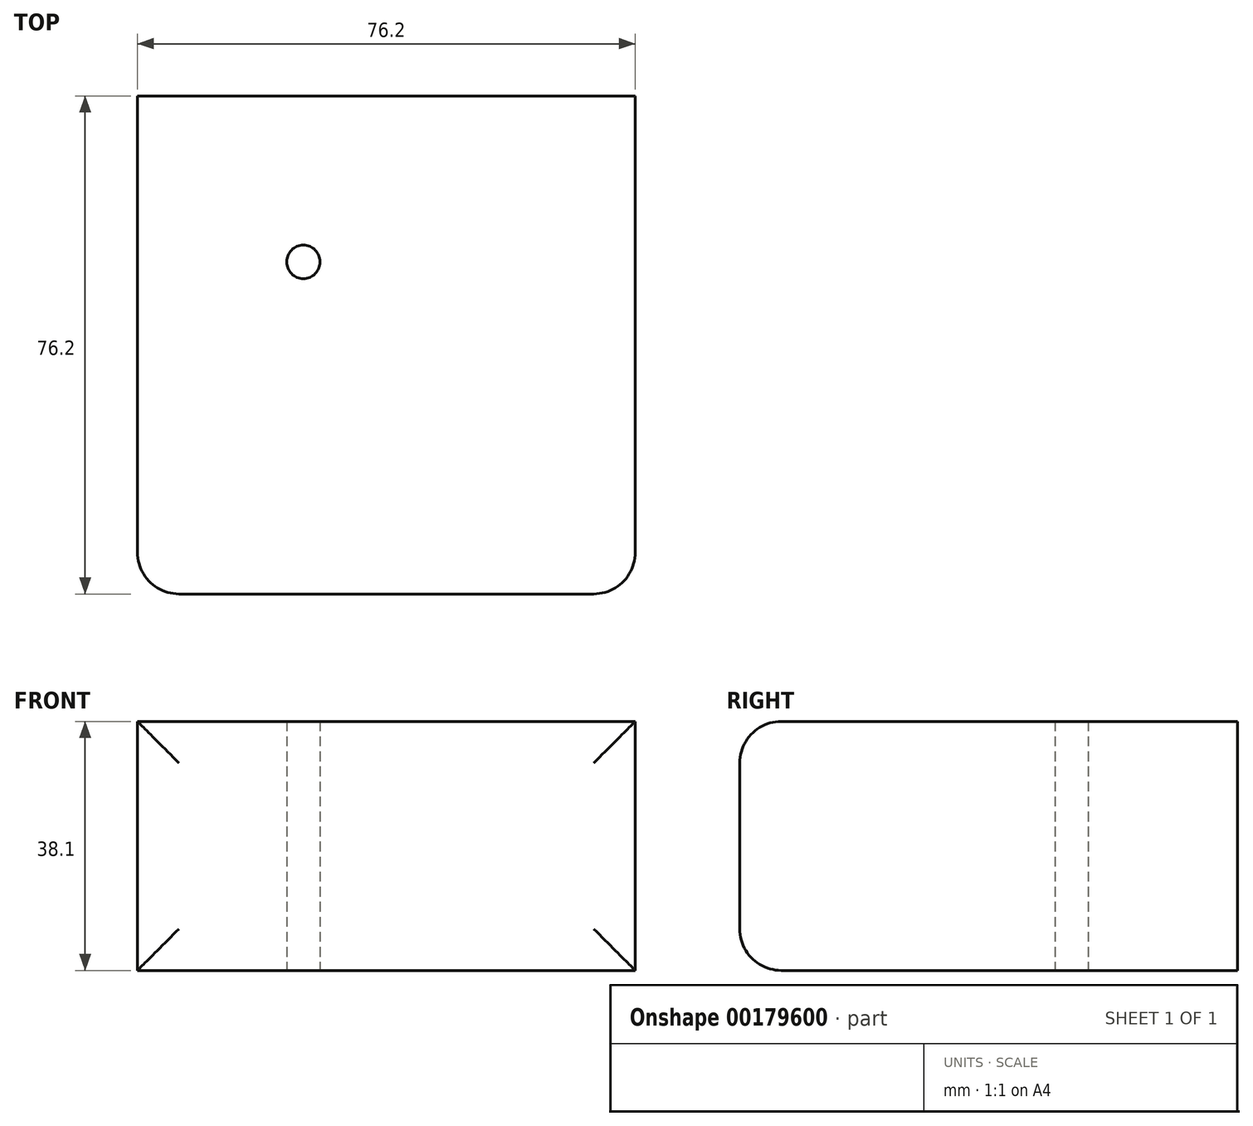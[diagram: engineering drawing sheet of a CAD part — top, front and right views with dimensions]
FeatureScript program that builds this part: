
annotation { "Feature Type Name" : "Feature", "Feature Type Description" : "" }
export const myFeature = defineFeature(function(context is Context, id is Id, definition is map)
    precondition{}
    {
        {
            var Q0;
            Q0=qCreatedBy(makeId("Front.planeOp"),FACE);
            var sketch = newSketch(context, id + "F0", { "sketchPlane" : qUnion([Q0])});
            skLineSegment(sketch, "E0.bottom", {"start": v(38.1, -19.05) * mm, "end": v(-38.1, -19.05) * mm});
            skLineSegment(sketch, "E0.top", {"start": v(38.1, 19.05) * mm, "end": v(-38.1, 19.05) * mm});
            skLineSegment(sketch, "E0.left", {"start": v(38.1, -19.05) * mm, "end": v(38.1, 19.05) * mm});
            skLineSegment(sketch, "E0.right", {"start": v(-38.1, -19.05) * mm, "end": v(-38.1, 19.05) * mm});
            skPoint(sketch, "E0.middle", {"position": v(0, 0) * mm});
            skSolve(sketch);
        }
        {
            var Q0;
            Q0 = qSketchRegion(id + "F0", true);
            extrude(context, id + "F1", {"entities" : qUnion([Q0]), "endBound" : BoundingType.SYMMETRIC, "depth" : 76.2 * mm});
        }
        {
            var Q0;
            Q0=makeQuery(id+"F1.opExtrude","CAP_EDGE",EDGE,{"disambiguationData":[OSD([sQuery(id+"F0.wireOp",EDGE,"E0.bottom")])],"isStart":false});
            var Q1;
            Q1=makeQuery(id+"F1.opExtrude","CAP_EDGE",EDGE,{"disambiguationData":[OSD([sQuery(id+"F0.wireOp",EDGE,"E0.top")])],"isStart":false});
            var Q2;
            Q2=makeQuery(id+"F1.opExtrude","CAP_EDGE",EDGE,{"disambiguationData":[OSD([sQuery(id+"F0.wireOp",EDGE,"E0.left")])],"isStart":false});
            var Q3;
            Q3=makeQuery(id+"F1.opExtrude","CAP_EDGE",EDGE,{"disambiguationData":[OSD([sQuery(id+"F0.wireOp",EDGE,"E0.right")])],"isStart":false});
            fillet(context, id + "F2", {"entities" : qUnion([Q0, Q1, Q2, Q3]), "radius" : 6.35 * mm, "tangentPropagation" : true, "allowEdgeOverflow" : false});
        }
        {
            var Q0;
            Q0=makeQuery(id+"F1.opExtrude","SWEPT_FACE",FACE,{"disambiguationData":[OSD([sQuery(id+"F0.wireOp",EDGE,"E0.bottom")])]});
            var sketch = newSketch(context, id + "F3", { "sketchPlane" : qUnion([Q0])});
            skPoint(sketch, "E1", {"position": v(-12.7, -12.7) * mm});
            skSolve(sketch);
        }
        {
            var Q0;
            Q0=sQuery(id+"F3.wireOp",VERTEX,"E1");
            var Q1;
            Q1=makeQuery(id+"F1.opExtrude","SWEPT_BODY",BODY,{"disambiguationData":[OSD([sQuery(id+"F0.wireOp",EDGE,"E0.bottom"),sQuery(id+"F0.wireOp",EDGE,"E0.top"),sQuery(id+"F0.wireOp",EDGE,"E0.left"),sQuery(id+"F0.wireOp",EDGE,"E0.right")])]});
            hole(context, id + "F4", {"style" : HoleStyle.SIMPLE, "endStyle" : HoleEndStyle.BLIND, "standardTappedOrClearance" : lookupTablePath({ "standard" : "ANSI", "engagement" : "75%", "pitch" : "20 tpi", "size" : "1/4", "type" : "Tapped" }), "standardBlindInLast" : lookupTablePath({ "standard" : "ANSI", "engagement" : "75%", "pitch" : "20 tpi", "size" : "1/4", "type" : "Tapped" }), "holeDiameter" : 5.1 * mm, "holeDepth" : 76.2 * mm, "locations" : qUnion([Q0]), "scope" : qUnion([Q1]), "majorDiameter" : 6.35 * mm});
        }
    });
